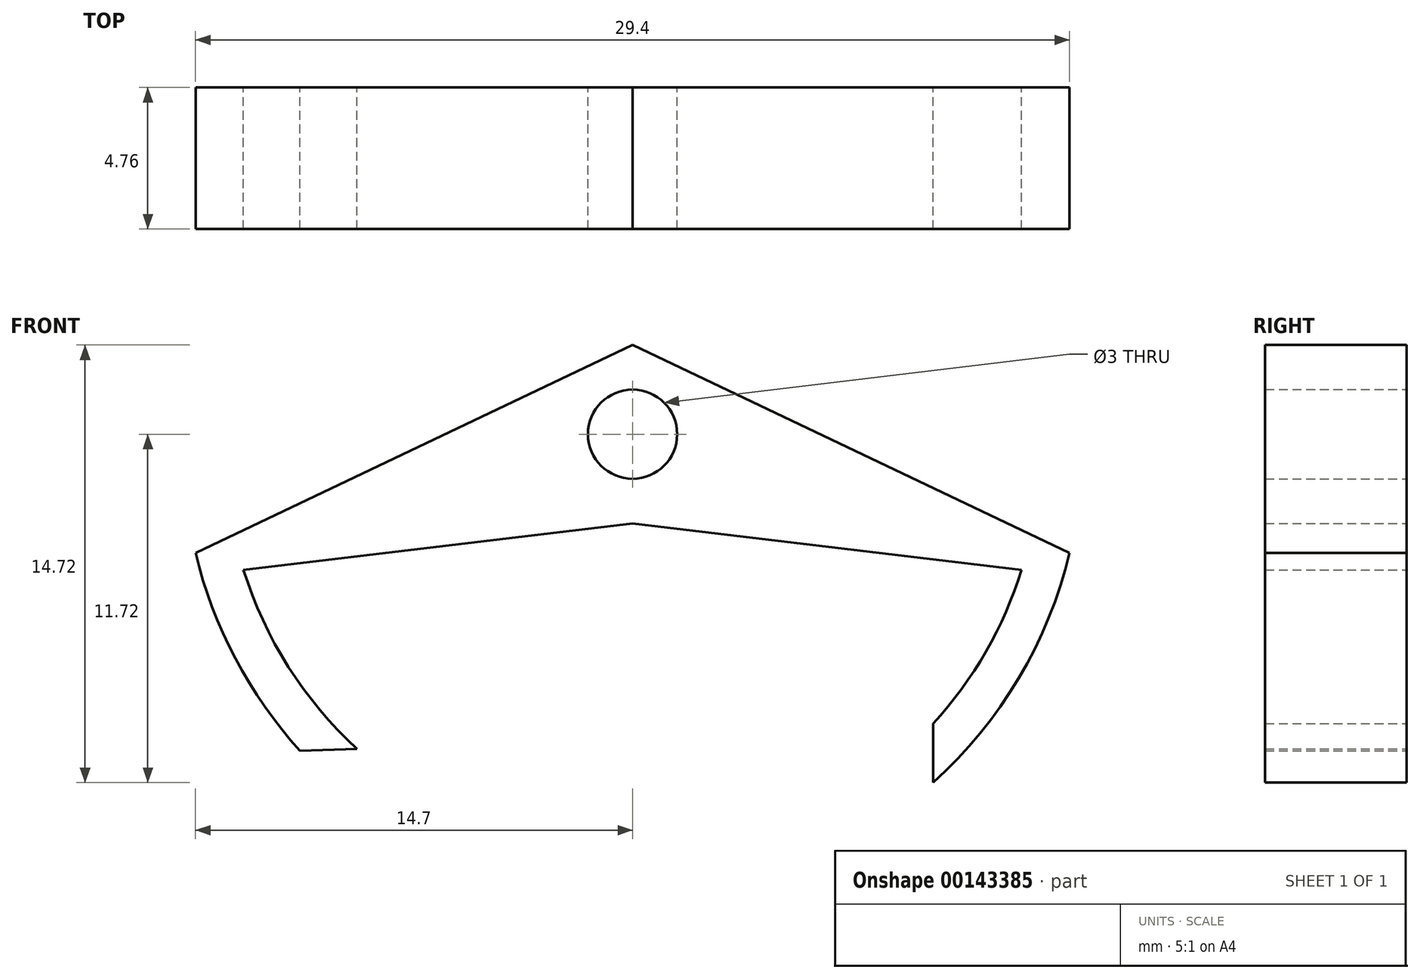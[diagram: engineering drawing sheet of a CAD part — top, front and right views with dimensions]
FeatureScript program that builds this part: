
annotation { "Feature Type Name" : "Feature", "Feature Type Description" : "" }
export const myFeature = defineFeature(function(context is Context, id is Id, definition is map)
    precondition{}
    {
        {
            var Q0;
            Q0=qCreatedBy(makeId("Front.planeOp"),FACE);
            var sketch = newSketch(context, id + "F0", { "sketchPlane" : qUnion([Q0])});
            skLineSegment(sketch, "E0", {"start": v(0, -0.48) * mm, "end": v(0, -0.48) * mm});
            skArc(sketch, "E1", {"start": v(10.1, -11.72) * mm, "mid": v(13, -8.2) * mm, "end": v(14.7, -4) * mm});
            skArc(sketch, "E2", {"start": v(10.1, -9.74) * mm, "mid": v(11.88, -7.31) * mm, "end": v(13.09, -4.56) * mm});
            skLineSegment(sketch, "E3", {"start": v(10.1, -9.74) * mm, "end": v(10.1, -11.72) * mm});
            skArc(sketch, "E4.trimOffspring", {"start": v(-13.09, -4.56) * mm, "mid": v(-11.58, -7.82) * mm, "end": v(-9.27, -10.58) * mm});
            skArc(sketch, "E5.trimOffspring", {"start": v(-14.7, -4) * mm, "mid": v(-13.36, -7.54) * mm, "end": v(-11.18, -10.65) * mm});
            skPoint(sketch, "E6.orphan", {"position": v(-14.43, -4.97) * mm});
            skPoint(sketch, "E7.orphan", {"position": v(14.43, -4.97) * mm});
            skCircle(sketch, "E8", {"center": v(0, 0) * mm, "radius": 1.5 * mm});
            skLineSegment(sketch, "E9", {"start": v(-13.09, -4.56) * mm, "end": v(0, -3) * mm});
            skLineSegment(sketch, "E10", {"start": v(0, -3) * mm, "end": v(13.09, -4.56) * mm});
            skLineSegment(sketch, "E11", {"start": v(-14.7, -4) * mm, "end": v(0, 3) * mm});
            skLineSegment(sketch, "E12", {"start": v(0, 3) * mm, "end": v(14.7, -4) * mm});
            skLineSegment(sketch, "E13", {"start": v(-11.18, -10.65) * mm, "end": v(-9.27, -10.58) * mm});
            skLineSegment(sketch, "E14", {"start": v(10.1, -11.72) * mm, "end": v(10.05, -9.95) * mm});
            skSolve(sketch);
        }
        {
            var Q0;
            Q0=qSketchRegion(id+"F0",true);
            extrude(context, id + "F1", {"entities" : qUnion([Q0]), "depth" : 4.76 * mm});
        }
    });
